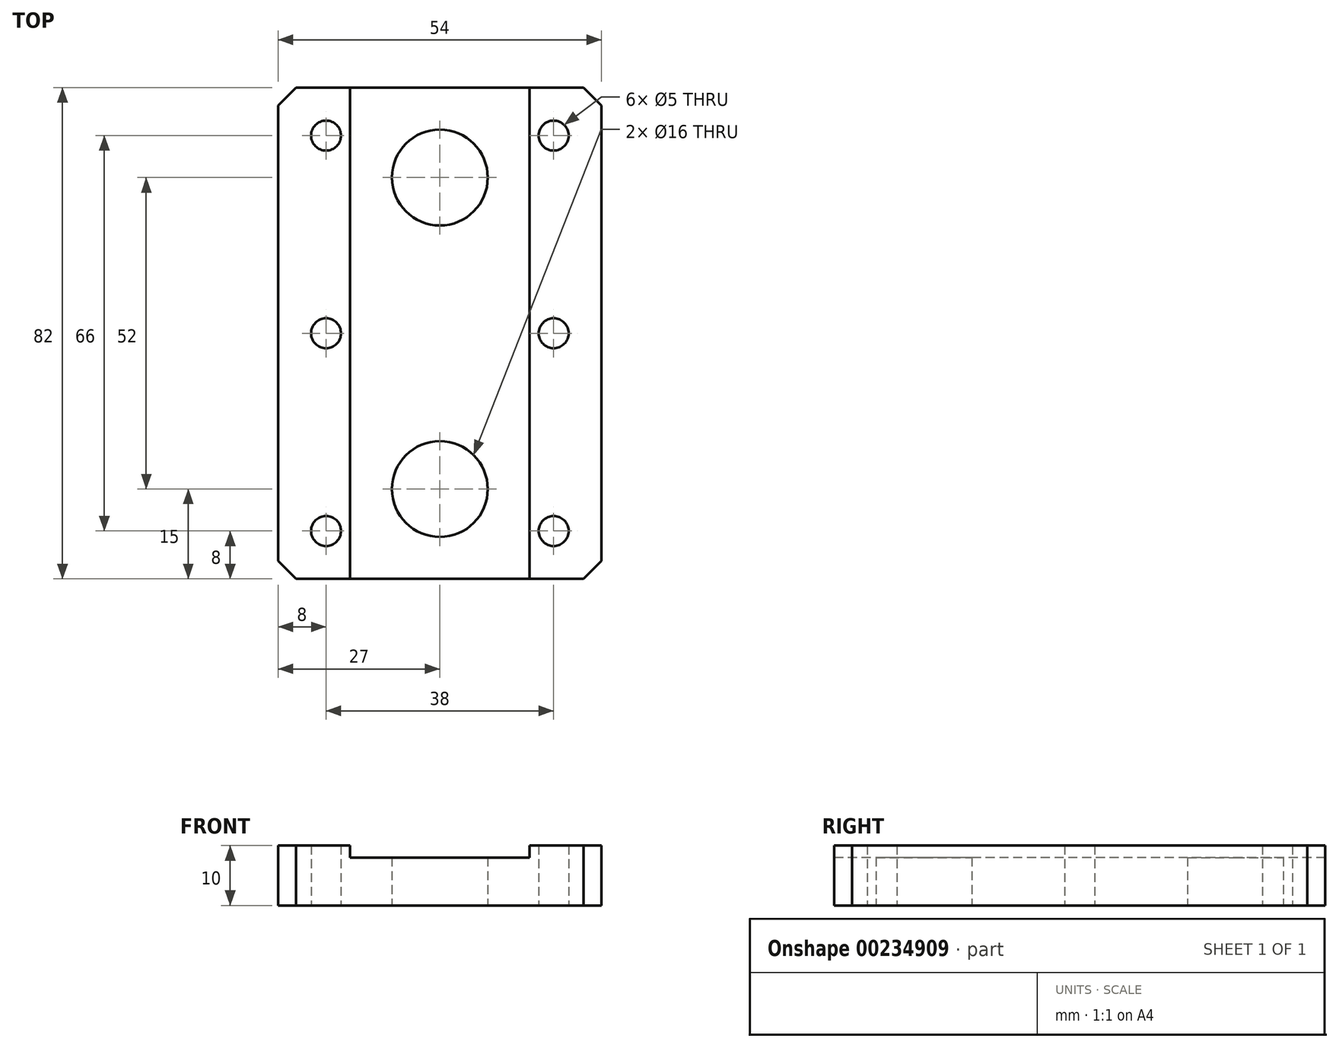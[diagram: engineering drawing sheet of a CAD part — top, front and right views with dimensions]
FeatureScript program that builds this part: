
annotation { "Feature Type Name" : "Feature", "Feature Type Description" : "" }
export const myFeature = defineFeature(function(context is Context, id is Id, definition is map)
    precondition{}
    {
        {
            var Q0;
            Q0=qCreatedBy(makeId("Top.planeOp"),FACE);
            var sketch = newSketch(context, id + "F0", { "sketchPlane" : qUnion([Q0])});
            skLineSegment(sketch, "E0.bottom", {"start": v(27, 41) * mm, "end": v(-27, 41) * mm});
            skLineSegment(sketch, "E0.top", {"start": v(27, -41) * mm, "end": v(-27, -41) * mm});
            skLineSegment(sketch, "E0.left", {"start": v(27, 41) * mm, "end": v(27, -41) * mm});
            skLineSegment(sketch, "E0.right", {"start": v(-27, 41) * mm, "end": v(-27, -41) * mm});
            skPoint(sketch, "E0.middle", {"position": v(0, 0) * mm});
            skLineSegment(sketch, "E1", {"start": v(0, 41) * mm, "end": v(0, -41) * mm, "construction": true});
            skLineSegment(sketch, "E2", {"start": v(-27, 0) * mm, "end": v(27, 0) * mm, "construction": true});
            skCircle(sketch, "E3", {"center": v(0, -26) * mm, "radius": 8 * mm});
            skCircle(sketch, "E4", {"center": v(0, 26) * mm, "radius": 8 * mm});
            skLineSegment(sketch, "E5", {"start": v(-19, 41) * mm, "end": v(-19, -41) * mm, "construction": true});
            skCircle(sketch, "E6", {"center": v(-19, 0) * mm, "radius": 2.5 * mm});
            skCircle(sketch, "E7", {"center": v(-19, 33) * mm, "radius": 2.5 * mm});
            skCircle(sketch, "E8", {"center": v(-19, -33) * mm, "radius": 2.5 * mm});
            skCircle(sketch, "E9.MirrorC", {"center": v(19, -33) * mm, "radius": 2.5 * mm});
            skCircle(sketch, "E10.MirrorC", {"center": v(19, 33) * mm, "radius": 2.5 * mm});
            skCircle(sketch, "E11.MirrorC", {"center": v(19, 0) * mm, "radius": 2.5 * mm});
            skSolve(sketch);
        }
        {
            var Q0;
            Q0 = qSketchRegion(id + "F0", true);
            extrude(context, id + "F1", {"entities" : qUnion([Q0]), "depth" : 10 * mm});
        }
        {
            var Q0;
            Q0=makeQuery(id+"F1.opExtrude","SWEPT_EDGE",EDGE,{"disambiguationData":[OSD([sQuery(id+"F0.wireOp",EDGE,"E0.top"),sQuery(id+"F0.wireOp",EDGE,"E0.left")])]});
            var Q1;
            Q1=makeQuery(id+"F1.opExtrude","SWEPT_EDGE",EDGE,{"disambiguationData":[OSD([sQuery(id+"F0.wireOp",EDGE,"E0.top"),sQuery(id+"F0.wireOp",EDGE,"E0.right")])]});
            var Q2;
            Q2=makeQuery(id+"F1.opExtrude","SWEPT_EDGE",EDGE,{"disambiguationData":[OSD([sQuery(id+"F0.wireOp",EDGE,"E0.bottom"),sQuery(id+"F0.wireOp",EDGE,"E0.left")])]});
            var Q3;
            Q3=makeQuery(id+"F1.opExtrude","SWEPT_EDGE",EDGE,{"disambiguationData":[OSD([sQuery(id+"F0.wireOp",EDGE,"E0.bottom"),sQuery(id+"F0.wireOp",EDGE,"E0.right")])]});
            chamfer(context, id + "F2", {"entities" : qUnion([Q0, Q1, Q2, Q3]), "width" : 3 * mm, "tangentPropagation" : true});
        }
        {
            var Q0;
            Q0=makeQuery(id+"F1.opExtrude","CAP_FACE",FACE,{"disambiguationData":[OSD([sQuery(id+"F0.wireOp",EDGE,"E0.bottom"),sQuery(id+"F0.wireOp",EDGE,"E0.top"),sQuery(id+"F0.wireOp",EDGE,"E0.left"),sQuery(id+"F0.wireOp",EDGE,"E0.right"),sQuery(id+"F0.wireOp",EDGE,"E3"),sQuery(id+"F0.wireOp",EDGE,"E4"),sQuery(id+"F0.wireOp",EDGE,"E8"),sQuery(id+"F0.wireOp",EDGE,"E6"),sQuery(id+"F0.wireOp",EDGE,"E7"),sQuery(id+"F0.wireOp",EDGE,"E9.MirrorC"),sQuery(id+"F0.wireOp",EDGE,"E10.MirrorC"),sQuery(id+"F0.wireOp",EDGE,"E11.MirrorC")])],"isStart":false});
            var sketch = newSketch(context, id + "F3", { "sketchPlane" : qUnion([Q0])});
            skLineSegment(sketch, "E12", {"start": v(0, 41) * mm, "end": v(0, -41) * mm, "construction": true});
            skLineSegment(sketch, "E13", {"start": v(-15, 41) * mm, "end": v(-15, -41) * mm});
            skLineSegment(sketch, "E14", {"start": v(15, 41) * mm, "end": v(15, -41) * mm});
            skLineSegment(sketch, "E15", {"start": v(-15, 41) * mm, "end": v(15, 41) * mm});
            skLineSegment(sketch, "E16", {"start": v(-15, -41) * mm, "end": v(15, -41) * mm});
            skSolve(sketch);
        }
        {
            var Q0;
            Q0 = qSketchRegion(id + "F3", true);
            extrude(context, id + "F4", {"entities" : qUnion([Q0]), "operationType" : NewBodyOperationType.REMOVE, "oppositeDirection" : true, "depth" : 2 * mm});
        }
    });
